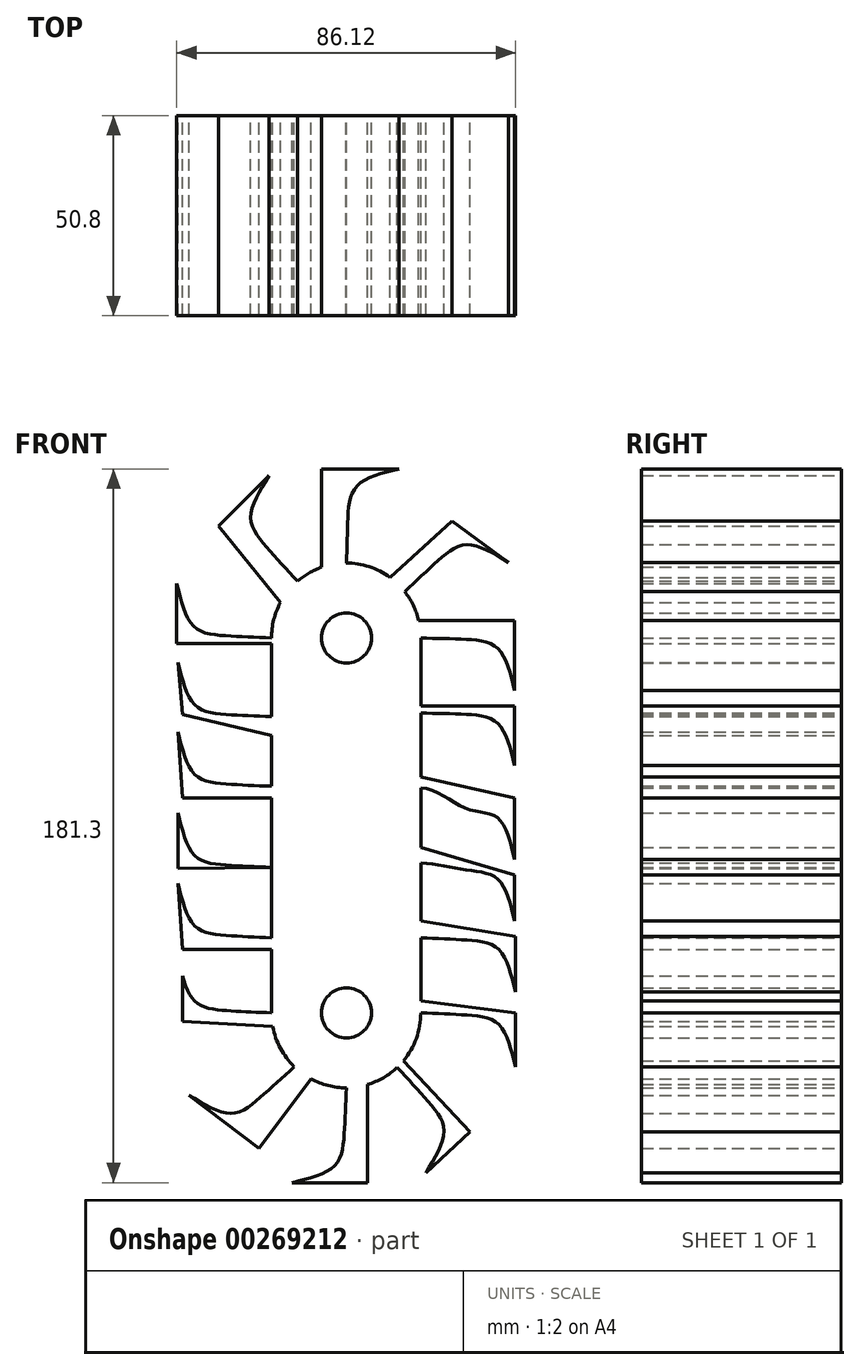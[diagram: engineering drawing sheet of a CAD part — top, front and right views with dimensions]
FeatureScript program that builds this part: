
annotation { "Feature Type Name" : "Feature", "Feature Type Description" : "" }
export const myFeature = defineFeature(function(context is Context, id is Id, definition is map)
    precondition{}
    {
        {
            var Q0;
            Q0=qCreatedBy(makeId("Front.planeOp"),FACE);
            var sketch = newSketch(context, id + "F0", { "sketchPlane" : qUnion([Q0])});
            skLineSegment(sketch, "E0.bottom", {"start": v(-0.09, 66.67) * mm, "end": v(0.09, 66.67) * mm});
            skLineSegment(sketch, "E0.top", {"start": v(-0.09, -66.68) * mm, "end": v(0.09, -66.68) * mm});
            skLineSegment(sketch, "E0.left", {"start": v(-18.96, 47.62) * mm, "end": v(-18.96, -47.62) * mm});
            skLineSegment(sketch, "E0.right", {"start": v(18.96, 47.62) * mm, "end": v(18.96, -47.62) * mm});
            skPoint(sketch, "E0.middle", {"position": v(0, 0) * mm});
            skFitSpline(sketch, "E1", {"points": [v(18.96, 47.62) * mm, v(30.75, 47.25) * mm, v(38.5, 44.95) * mm, v(42.82, 34.32) * mm], "startDerivative": vector(34.19, -1.32) * mm, "endDerivative": vector(8.67, -36.4) * mm});
            skFitSpline(sketch, "E2", {"points": [v(18.96, 28.57) * mm, v(30.75, 28.2) * mm, v(38.5, 25.9) * mm, v(42.82, 15.27) * mm], "startDerivative": vector(34.19, -1.32) * mm, "endDerivative": vector(8.67, -36.4) * mm});
            skFitSpline(sketch, "E3", {"points": [v(18.96, 9.52) * mm, v(30.74, 4.22) * mm, v(38.5, 1.92) * mm, v(42.8, -8.7) * mm], "startDerivative": vector(34.19, -1.31) * mm, "endDerivative": vector(8.71, -36.4) * mm});
            skFitSpline(sketch, "E4", {"points": [v(18.96, -9.53) * mm, v(30.74, -11.34) * mm, v(38.5, -13.64) * mm, v(42.8, -24.27) * mm], "startDerivative": vector(34.19, -1.31) * mm, "endDerivative": vector(8.71, -36.4) * mm});
            skFitSpline(sketch, "E5", {"points": [v(18.96, -28.58) * mm, v(30.86, -29.17) * mm, v(38.74, -31.51) * mm, v(43.06, -42.36) * mm], "startDerivative": vector(34.97, -1.3) * mm, "endDerivative": vector(9.95, -36.94) * mm});
            skFitSpline(sketch, "E6", {"points": [v(18.96, -47.62) * mm, v(30.86, -48.22) * mm, v(38.74, -50.56) * mm, v(43.06, -61.41) * mm], "startDerivative": vector(34.97, -1.3) * mm, "endDerivative": vector(9.95, -36.94) * mm});
            skPoint(sketch, "E7.visualSharp", {"position": v(-18.96, 66.68) * mm});
            skArc(sketch, "E7.filletArc", {"start": v(0.09, 66.67) * mm, "mid": v(-13.38, 61.1) * mm, "end": v(-18.96, 47.62) * mm});
            skPoint(sketch, "E8.visualSharp", {"position": v(18.96, 66.67) * mm});
            skArc(sketch, "E8.filletArc", {"start": v(18.96, 47.62) * mm, "mid": v(13.38, 61.1) * mm, "end": v(-0.09, 66.67) * mm});
            skPoint(sketch, "E9.visualSharp", {"position": v(-18.96, -66.67) * mm});
            skArc(sketch, "E9.filletArc", {"start": v(-18.96, -47.62) * mm, "mid": v(-13.38, -61.1) * mm, "end": v(0.09, -66.67) * mm});
            skPoint(sketch, "E10.visualSharp", {"position": v(18.96, -66.68) * mm});
            skArc(sketch, "E10.filletArc", {"start": v(-0.09, -66.67) * mm, "mid": v(13.38, -61.1) * mm, "end": v(18.96, -47.62) * mm});
            skFitSpline(sketch, "E11", {"points": [v(0.09, 66.67) * mm, v(0.46, 78.46) * mm, v(2.76, 86.22) * mm, v(13.4, 90.53) * mm], "startDerivative": vector(1.32, 34.19) * mm, "endDerivative": vector(36.4, 8.67) * mm});
            skFitSpline(sketch, "E12", {"points": [v(14.9, 59.38) * mm, v(23.5, 67.45) * mm, v(30.62, 71.3) * mm, v(41.18, 66.84) * mm], "startDerivative": vector(25.1, 23.24) * mm, "endDerivative": vector(31.87, -19.6) * mm});
            skFitSpline(sketch, "E13", {"points": [v(0.08, -66.67) * mm, v(-0.51, -78.57) * mm, v(-2.86, -86.45) * mm, v(-13.7, -90.77) * mm], "startDerivative": vector(-1.3, -34.97) * mm, "endDerivative": vector(-36.94, -9.95) * mm});
            skFitSpline(sketch, "E14", {"points": [v(12.98, -61.49) * mm, v(20.97, -70.32) * mm, v(24.89, -77.55) * mm, v(20.27, -88.27) * mm], "startDerivative": vector(23.8, -25.65) * mm, "endDerivative": vector(-19.08, -33.15) * mm});
            skFitSpline(sketch, "E15", {"points": [v(-18.64, -47.63) * mm, v(-30.54, -47.03) * mm, v(-38.42, -44.69) * mm, v(-42.74, -33.84) * mm], "startDerivative": vector(-34.97, 1.3) * mm, "endDerivative": vector(-9.95, 36.94) * mm});
            skFitSpline(sketch, "E16", {"points": [v(-12.36, 62.05) * mm, v(-20.36, 70.88) * mm, v(-24.27, 78.1) * mm, v(-19.65, 88.83) * mm], "startDerivative": vector(-23.8, 25.65) * mm, "endDerivative": vector(19.08, 33.15) * mm});
            skFitSpline(sketch, "E17", {"points": [v(-13.18, -61.3) * mm, v(-22.01, -69.29) * mm, v(-29.24, -73.2) * mm, v(-39.97, -68.58) * mm], "startDerivative": vector(-25.65, -23.8) * mm, "endDerivative": vector(-33.15, 19.08) * mm});
            skFitSpline(sketch, "E18", {"points": [v(-18.96, 47.62) * mm, v(-30.86, 48.22) * mm, v(-38.74, 50.56) * mm, v(-43.06, 61.41) * mm], "startDerivative": vector(-34.97, 1.3) * mm, "endDerivative": vector(-9.95, 36.94) * mm});
            skFitSpline(sketch, "E19", {"points": [v(-18.64, -28.55) * mm, v(-30.54, -27.96) * mm, v(-38.42, -25.61) * mm, v(-42.74, -14.76) * mm], "startDerivative": vector(-34.97, 1.3) * mm, "endDerivative": vector(-9.95, 36.94) * mm});
            skFitSpline(sketch, "E20", {"points": [v(-18.64, 9.94) * mm, v(-30.54, 10.54) * mm, v(-38.42, 12.88) * mm, v(-42.74, 23.73) * mm], "startDerivative": vector(-34.97, 1.3) * mm, "endDerivative": vector(-9.95, 36.94) * mm});
            skFitSpline(sketch, "E21", {"points": [v(-18.64, -10.67) * mm, v(-30.54, -10.07) * mm, v(-38.42, -7.73) * mm, v(-42.74, 3.12) * mm], "startDerivative": vector(-34.97, 1.3) * mm, "endDerivative": vector(-9.95, 36.94) * mm});
            skFitSpline(sketch, "E22", {"points": [v(-18.64, 27.6) * mm, v(-30.54, 28.2) * mm, v(-38.42, 30.55) * mm, v(-42.74, 41.4) * mm], "startDerivative": vector(-34.97, 1.3) * mm, "endDerivative": vector(-9.95, 36.94) * mm});
            skLineSegment(sketch, "E23", {"start": v(43.06, -42.36) * mm, "end": v(43.06, -28.23) * mm});
            skLineSegment(sketch, "E24", {"start": v(43.06, -28.23) * mm, "end": v(18.96, -24.27) * mm});
            skLineSegment(sketch, "E25", {"start": v(42.8, -24.27) * mm, "end": v(42.8, -12.64) * mm});
            skLineSegment(sketch, "E26", {"start": v(42.8, -12.64) * mm, "end": v(18.96, -5.57) * mm});
            skLineSegment(sketch, "E27", {"start": v(42.8, -8.7) * mm, "end": v(42.8, 6.96) * mm});
            skLineSegment(sketch, "E28", {"start": v(42.8, 6.96) * mm, "end": v(18.96, 12.27) * mm});
            skLineSegment(sketch, "E29", {"start": v(42.82, 15.27) * mm, "end": v(42.82, 30.4) * mm});
            skLineSegment(sketch, "E30", {"start": v(42.82, 30.4) * mm, "end": v(18.96, 30.4) * mm});
            skLineSegment(sketch, "E31", {"start": v(41.18, 66.84) * mm, "end": v(26.85, 77.27) * mm});
            skLineSegment(sketch, "E32", {"start": v(26.85, 77.27) * mm, "end": v(11.12, 63.03) * mm});
            skLineSegment(sketch, "E33", {"start": v(13.4, 90.53) * mm, "end": v(-6.2, 90.53) * mm});
            skLineSegment(sketch, "E34", {"start": v(-6.2, 90.53) * mm, "end": v(-6.2, 65.6) * mm});
            skLineSegment(sketch, "E35", {"start": v(-19.65, 88.83) * mm, "end": v(-32.44, 76.05) * mm});
            skLineSegment(sketch, "E36", {"start": v(-32.44, 76.05) * mm, "end": v(-16.72, 56.6) * mm});
            skLineSegment(sketch, "E37", {"start": v(-43.06, 61.41) * mm, "end": v(-43.06, 46.24) * mm});
            skLineSegment(sketch, "E38", {"start": v(-43.06, 46.24) * mm, "end": v(-18.96, 46.24) * mm});
            skLineSegment(sketch, "E39", {"start": v(-42.74, 41.4) * mm, "end": v(-41.57, 28.2) * mm});
            skLineSegment(sketch, "E40", {"start": v(-41.57, 28.2) * mm, "end": v(-18.96, 22.86) * mm});
            skLineSegment(sketch, "E41", {"start": v(-42.74, 23.73) * mm, "end": v(-41.57, 6.96) * mm});
            skLineSegment(sketch, "E42", {"start": v(-41.57, 6.96) * mm, "end": v(-18.96, 6.96) * mm});
            skLineSegment(sketch, "E43", {"start": v(-42.74, 3.12) * mm, "end": v(-42.74, -10.95) * mm});
            skLineSegment(sketch, "E44", {"start": v(-42.74, -10.95) * mm, "end": v(-18.64, -10.67) * mm});
            skLineSegment(sketch, "E45", {"start": v(-42.74, -14.76) * mm, "end": v(-41.57, -31.54) * mm});
            skLineSegment(sketch, "E46", {"start": v(-41.57, -31.54) * mm, "end": v(-18.96, -31.54) * mm});
            skLineSegment(sketch, "E47", {"start": v(-41.57, -38.16) * mm, "end": v(-41.57, -49.78) * mm});
            skLineSegment(sketch, "E48", {"start": v(-41.57, -49.78) * mm, "end": v(-18.64, -51.1) * mm});
            skLineSegment(sketch, "E49", {"start": v(-39.97, -68.58) * mm, "end": v(-22.1, -82) * mm});
            skLineSegment(sketch, "E50", {"start": v(-22.1, -82) * mm, "end": v(-8.9, -64.42) * mm});
            skLineSegment(sketch, "E51", {"start": v(-13.7, -90.77) * mm, "end": v(5.46, -90.77) * mm});
            skLineSegment(sketch, "E52", {"start": v(5.46, -90.77) * mm, "end": v(5.46, -65.85) * mm});
            skLineSegment(sketch, "E53", {"start": v(43.06, -61.41) * mm, "end": v(43.06, -47.58) * mm});
            skLineSegment(sketch, "E54", {"start": v(43.06, -47.58) * mm, "end": v(18.96, -44.64) * mm});
            skLineSegment(sketch, "E55", {"start": v(20.27, -88.27) * mm, "end": v(31.43, -77.83) * mm});
            skLineSegment(sketch, "E56", {"start": v(31.43, -77.83) * mm, "end": v(14.56, -59.8) * mm});
            skLineSegment(sketch, "E57", {"start": v(42.82, 34.32) * mm, "end": v(42.82, 52.07) * mm});
            skLineSegment(sketch, "E58", {"start": v(42.82, 52.07) * mm, "end": v(18.44, 52.07) * mm});
            skCircle(sketch, "E59", {"center": v(0.09, 47.62) * mm, "radius": 6.35 * mm});
            skCircle(sketch, "E60", {"center": v(0.09, -47.62) * mm, "radius": 6.35 * mm});
            skSolve(sketch);
        }
        {
            var Q0;
            Q0 = qSketchRegion(id + "F0", true);
            extrude(context, id + "F1", {"entities" : qUnion([Q0]), "depth" : 50.8 * mm});
        }
    });
